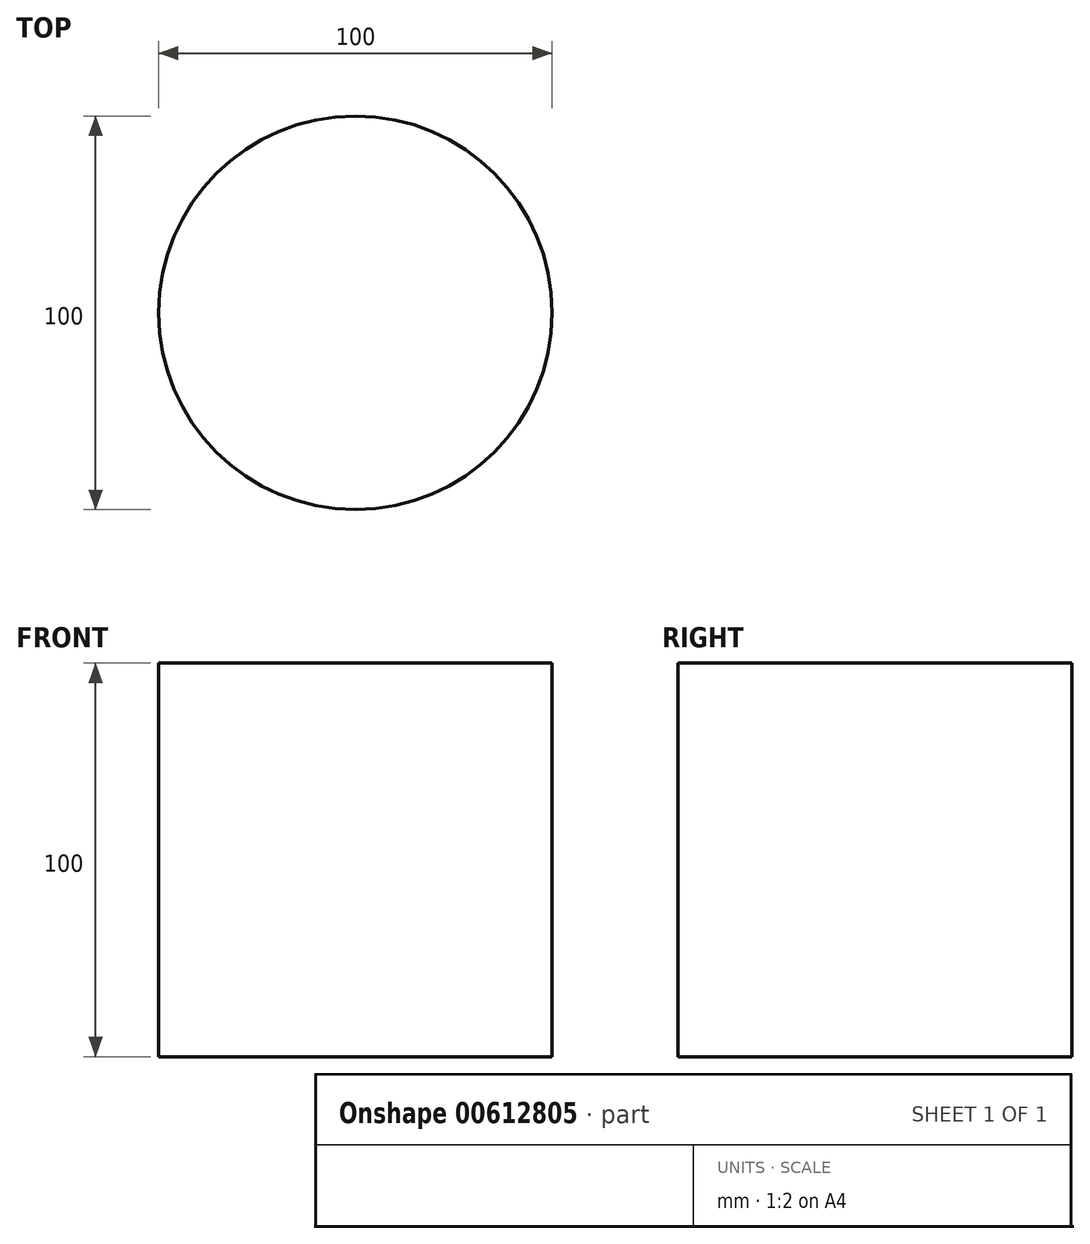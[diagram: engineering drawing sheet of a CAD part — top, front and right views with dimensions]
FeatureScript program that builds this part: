
annotation { "Feature Type Name" : "Feature", "Feature Type Description" : "" }
export const myFeature = defineFeature(function(context is Context, id is Id, definition is map)
    precondition{}
    {
        {
            var Q0;
            Q0=qCreatedBy(makeId("Top.planeOp"),FACE);
            var sketch = newSketch(context, id + "F0", { "sketchPlane" : qUnion([Q0])});
            skCircle(sketch, "E0", {"center": v(-25.1, 33.36) * mm, "radius": 50 * mm});
            skSolve(sketch);
        }
        {
            var Q0;
            Q0=makeQuery(id+"F0.imprint","IMPRINT",FACE,{"disambiguationData":[TD([[makeQuery(id+"F0.imprint","IMPRINT",EDGE,{"derivedFrom":sQuery(id+"F0.wireOp",EDGE,"E0")}),1.0]])]});
            extrude(context, id + "F1", {"entities" : qUnion([Q0]), "depth" : 100 * mm, "offsetDistance" : 25 * mm});
        }
    });
